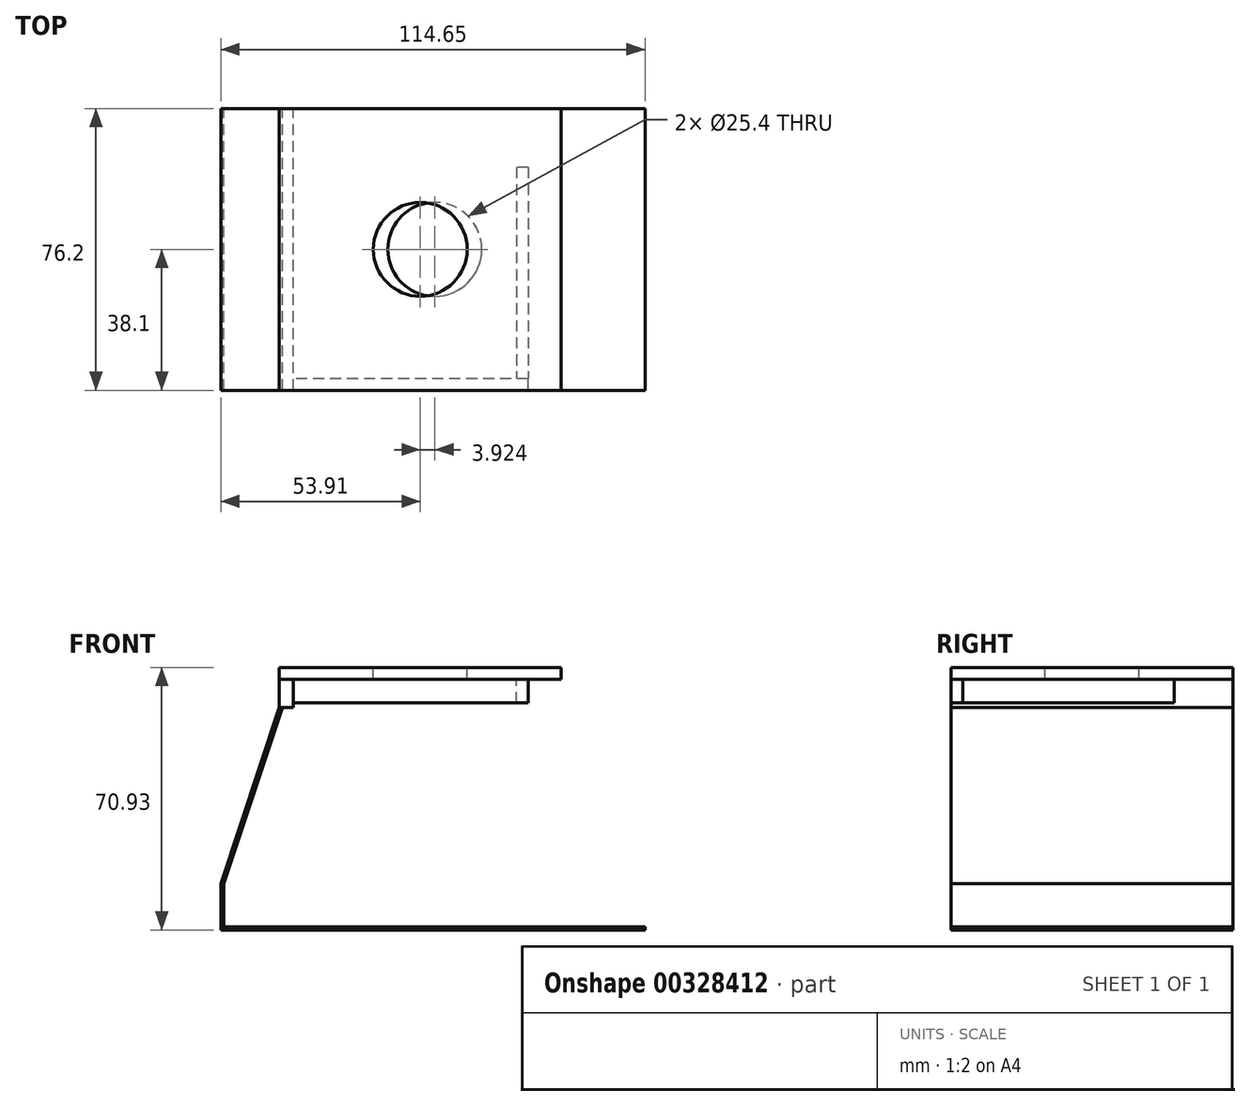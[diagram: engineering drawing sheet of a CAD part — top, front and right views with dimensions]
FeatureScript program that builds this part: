
annotation { "Feature Type Name" : "Feature", "Feature Type Description" : "" }
export const myFeature = defineFeature(function(context is Context, id is Id, definition is map)
    precondition{}
    {
        {
            var Q0;
            Q0=qCreatedBy(makeId("Top.planeOp"),FACE);
            var sketch = newSketch(context, id + "F0", { "sketchPlane" : qUnion([Q0])});
            skLineSegment(sketch, "E0.bottom", {"start": v(0, 0) * mm, "end": v(76.2, 0) * mm});
            skLineSegment(sketch, "E0.top", {"start": v(0, 76.2) * mm, "end": v(76.2, 76.2) * mm});
            skLineSegment(sketch, "E0.left", {"start": v(0, 0) * mm, "end": v(0, 76.2) * mm});
            skLineSegment(sketch, "E0.right", {"start": v(76.2, 0) * mm, "end": v(76.2, 76.2) * mm});
            skSolve(sketch);
        }
        {
            var Q0;
            Q0=makeQuery(id+"F0.imprint","IMPRINT",FACE,{"disambiguationData":[TD([[makeQuery(id+"F0.imprint","IMPRINT",EDGE,{"derivedFrom":sQuery(id+"F0.wireOp",EDGE,"E0.bottom")}),1.0]])]});
            extrude(context, id + "F1", {"entities" : qUnion([Q0]), "depth" : 3.17 * mm});
        }
        {
            var Q0;
            Q0=makeQuery(id+"F1.opExtrude","CAP_FACE",FACE,{"disambiguationData":[OSD([sQuery(id+"F0.wireOp",EDGE,"E0.bottom"),sQuery(id+"F0.wireOp",EDGE,"E0.top"),sQuery(id+"F0.wireOp",EDGE,"E0.left"),sQuery(id+"F0.wireOp",EDGE,"E0.right")])],"isStart":false});
            var sketch = newSketch(context, id + "F2", { "sketchPlane" : qUnion([Q0])});
            skPoint(sketch, "E1", {"position": v(38.1, 76.2) * mm});
            skPoint(sketch, "E2", {"position": v(38.1, 0) * mm});
            skPoint(sketch, "E3", {"position": v(0, 38.1) * mm});
            skPoint(sketch, "E4", {"position": v(76.2, 38.1) * mm});
            skLineSegment(sketch, "E5", {"start": v(38.1, 76.2) * mm, "end": v(38.1, 0) * mm, "construction": true});
            skCircle(sketch, "E6", {"center": v(38.1, 38.1) * mm, "radius": 12.7 * mm});
            skSolve(sketch);
        }
        {
            var Q0;
            Q0 = qSketchRegion(id + "F2", true);
            extrude(context, id + "F3", {"entities" : qUnion([Q0]), "operationType" : NewBodyOperationType.REMOVE, "endBound" : BoundingType.THROUGH_ALL, "oppositeDirection" : true, "depth" : 25.4 * mm});
        }
        {
            var Q0;
            Q0=makeQuery(id+"F1.opExtrude","SWEPT_FACE",FACE,{"disambiguationData":[OSD([sQuery(id+"F0.wireOp",EDGE,"E0.left")])]});
            var sketch = newSketch(context, id + "F4", { "sketchPlane" : qUnion([Q0])});
            skLineSegment(sketch, "E7", {"start": v(-76.2, 0) * mm, "end": v(-76.2, -7.62) * mm});
            skLineSegment(sketch, "E8", {"start": v(-76.2, -7.62) * mm, "end": v(0, -7.62) * mm});
            skLineSegment(sketch, "E9", {"start": v(0, -7.62) * mm, "end": v(0, 0) * mm});
            skLineSegment(sketch, "E10", {"start": v(-76.2, 0) * mm, "end": v(0, 0) * mm});
            skSolve(sketch);
        }
        {
            var Q0;
            Q0 = qSketchRegion(id + "F4", true);
            var Q1;
            Q1=makeQuery(id+"F4.imprint","IMPRINT",FACE,{"disambiguationData":[TD([[makeQuery(id+"F4.imprint","IMPRINT",EDGE,{"derivedFrom":sQuery(id+"F4.wireOp",EDGE,"xhthotyZ-Ec8U-3al9-CUq6-dATW5L7fGSU6")}),1.0]])]});
            extrude(context, id + "F5", {"entities" : qUnion([Q0, Q1]), "oppositeDirection" : true, "depth" : 3.8 * mm});
        }
        {
            var Q0;
            Q0 = qBodyType(qCreatedBy(id + "F7" ,EDGE), BodyType.WIRE);
            var Q1;
            Q1=makeQuery(id+"F5.opExtrude","CAP_FACE",FACE,{"disambiguationData":[OSD([sQuery(id+"F4.wireOp",EDGE,"E7"),sQuery(id+"F4.wireOp",EDGE,"E8"),sQuery(id+"F4.wireOp",EDGE,"E9"),sQuery(id+"F4.wireOp",EDGE,"E10")])],"isStart":false});
            cPlane(context, id + "F6", {"entities" : qUnion([Q0, Q1]), "cplaneType" : CPlaneType.OFFSET, "offset" : 0 * mm, "width" : 152.4 * mm, "height" : 152.4 * mm});
        }
        {
            var Q0;
            Q0=qCreatedBy(id+"F6.planeOp",FACE);
            var sketch = newSketch(context, id + "F7", { "sketchPlane" : qUnion([Q0])});
            skLineSegment(sketch, "E11.bottom", {"start": v(0, 0) * mm, "end": v(3.18, 0) * mm});
            skLineSegment(sketch, "E11.top", {"start": v(0, -6.35) * mm, "end": v(3.18, -6.35) * mm});
            skLineSegment(sketch, "E11.left", {"start": v(0, 0) * mm, "end": v(0, -6.35) * mm});
            skLineSegment(sketch, "E11.right", {"start": v(3.18, 0) * mm, "end": v(3.18, -6.35) * mm});
            skSolve(sketch);
        }
        {
            var Q0;
            Q0=makeQuery(id+"F7.imprint","IMPRINT",FACE,{"disambiguationData":[TD([[makeQuery(id+"F7.imprint","IMPRINT",EDGE,{"derivedFrom":sQuery(id+"F7.wireOp",EDGE,"E11.bottom")}),-1.0]])]});
            extrude(context, id + "F8", {"entities" : qUnion([Q0]), "depth" : 63.5 * mm});
        }
        {
            var Q0;
            Q0=makeQuery(id+"F5.opExtrude","SWEPT_FACE",FACE,{"disambiguationData":[OSD([sQuery(id+"F4.wireOp",EDGE,"E8")])]});
            cPlane(context, id + "F9", {"entities" : qUnion([Q0]), "cplaneType" : CPlaneType.OFFSET, "offset" : 60.27 * mm, "width" : 152.4 * mm, "height" : 152.4 * mm});
        }
        {
            var Q0;
            Q0=qCreatedBy(id+"F9.planeOp",FACE);
            var sketch = newSketch(context, id + "F10", { "sketchPlane" : qUnion([Q0])});
            skSolve(sketch);
        }
        {
            var Q0;
            Q0=makeQuery(id+"F5.opExtrude","SWEPT_FACE",FACE,{"disambiguationData":[OSD([sQuery(id+"F4.wireOp",EDGE,"E7")])]});
            var sketch = newSketch(context, id + "F11", { "sketchPlane" : qUnion([Q0])});
            skLineSegment(sketch, "E12", {"start": v(0, -7.62) * mm, "end": v(-0.8, -7.62) * mm});
            skLineSegment(sketch, "E13", {"start": v(-0.8, -7.62) * mm, "end": v(15.02, -55.26) * mm});
            skLineSegment(sketch, "E14", {"start": v(0, -7.62) * mm, "end": v(15.81, -55.26) * mm});
            skLineSegment(sketch, "E15", {"start": v(15.02, -55.26) * mm, "end": v(15.02, -66.95) * mm});
            skLineSegment(sketch, "E16", {"start": v(15.81, -67.75) * mm, "end": v(15.02, -67.75) * mm});
            skLineSegment(sketch, "E17", {"start": v(15.81, -55.26) * mm, "end": v(15.81, -67.75) * mm});
            skLineSegment(sketch, "E18", {"start": v(15.02, -67.75) * mm, "end": v(-98.83, -67.75) * mm});
            skLineSegment(sketch, "E19", {"start": v(15.02, -66.95) * mm, "end": v(-98.84, -66.95) * mm});
            skLineSegment(sketch, "E20", {"start": v(-98.83, -67.75) * mm, "end": v(-98.84, -66.95) * mm});
            skLineSegment(sketch, "E21", {"start": v(15.02, -66.95) * mm, "end": v(15.02, -67.75) * mm});
            skSolve(sketch);
        }
        {
            var Q0;
            Q0=makeQuery(id+"F11.imprint","IMPRINT",FACE,{"disambiguationData":[TD([[makeQuery(id+"F11.imprint","IMPRINT",EDGE,{"derivedFrom":sQuery(id+"F11.wireOp",EDGE,"Grh4E5rI-WkUZ-sssJ-0hTc-5guPxj1qBeTB")}),1.0]])]});
            var Q1;
            {var subQ3=sQuery(id+"F11.wireOp",EDGE,"E12");Q1=makeQuery(id+"F11.imprint","IMPRINT",FACE,{"disambiguationData":[TD([[makeQuery(id+"F11.imprint","IMPRINT",EDGE,{"derivedFrom":subQ3}),-1.0]])]});}
            extrude(context, id + "F12", {"entities" : qUnion([Q0, Q1]), "oppositeDirection" : true, "depth" : 76.2 * mm});
        }
        {
            var Q0;
            Q0=makeQuery(id+"F11.imprint","IMPRINT",FACE,{"disambiguationData":[TD([[makeQuery(id+"F11.imprint","IMPRINT",EDGE,{"derivedFrom":sQuery(id+"F11.wireOp",EDGE,"E18")}),-1.0]])]});
            var Q1;
            Q1 = qSketchRegion(id + "F10", true);
            extrude(context, id + "F13", {"entities" : qUnion([Q0, Q1]), "oppositeDirection" : true, "depth" : 76.2 * mm});
        }
        {
            var Q0;
            Q0=makeQuery(id+"F13.opExtrude","SWEPT_FACE",FACE,{"disambiguationData":[OSD([sQuery(id+"F11.wireOp",EDGE,"E19")])]});
            var sketch = newSketch(context, id + "F14", { "sketchPlane" : qUnion([Q0])});
            skCircle(sketch, "E22", {"center": v(42.02, 38.1) * mm, "radius": 12.7 * mm});
            skSolve(sketch);
        }
        {
            var Q0;
            Q0 = qSketchRegion(id + "F14", true);
            extrude(context, id + "F15", {"entities" : qUnion([Q0]), "operationType" : NewBodyOperationType.REMOVE, "endBound" : BoundingType.THROUGH_ALL, "oppositeDirection" : true, "depth" : 25.4 * mm});
        }
        {
            var Q0;
            Q0=makeQuery(id+"F8.opExtrude","SWEPT_FACE",FACE,{"disambiguationData":[OSD([sQuery(id+"F7.wireOp",EDGE,"E11.right")])]});
            var sketch = newSketch(context, id + "F16", { "sketchPlane" : qUnion([Q0])});
            skLineSegment(sketch, "E23", {"start": v(-67.3, 0) * mm, "end": v(-67.3, -6.35) * mm});
            skLineSegment(sketch, "E24", {"start": v(-67.3, -6.35) * mm, "end": v(-64.13, -6.35) * mm});
            skLineSegment(sketch, "E25", {"start": v(-64.13, -6.35) * mm, "end": v(-64.13, 0) * mm});
            skLineSegment(sketch, "E26", {"start": v(-64.13, 0) * mm, "end": v(-67.3, 0) * mm});
            skSolve(sketch);
        }
        {
            var Q0;
            Q0=makeQuery(id+"F16.imprint","IMPRINT",FACE,{"disambiguationData":[TD([[makeQuery(id+"F16.imprint","IMPRINT",EDGE,{"derivedFrom":sQuery(id+"F16.wireOp",EDGE,"E23")}),1.0]])]});
            extrude(context, id + "F17", {"entities" : qUnion([Q0]), "depth" : 57.15 * mm});
        }
    });
